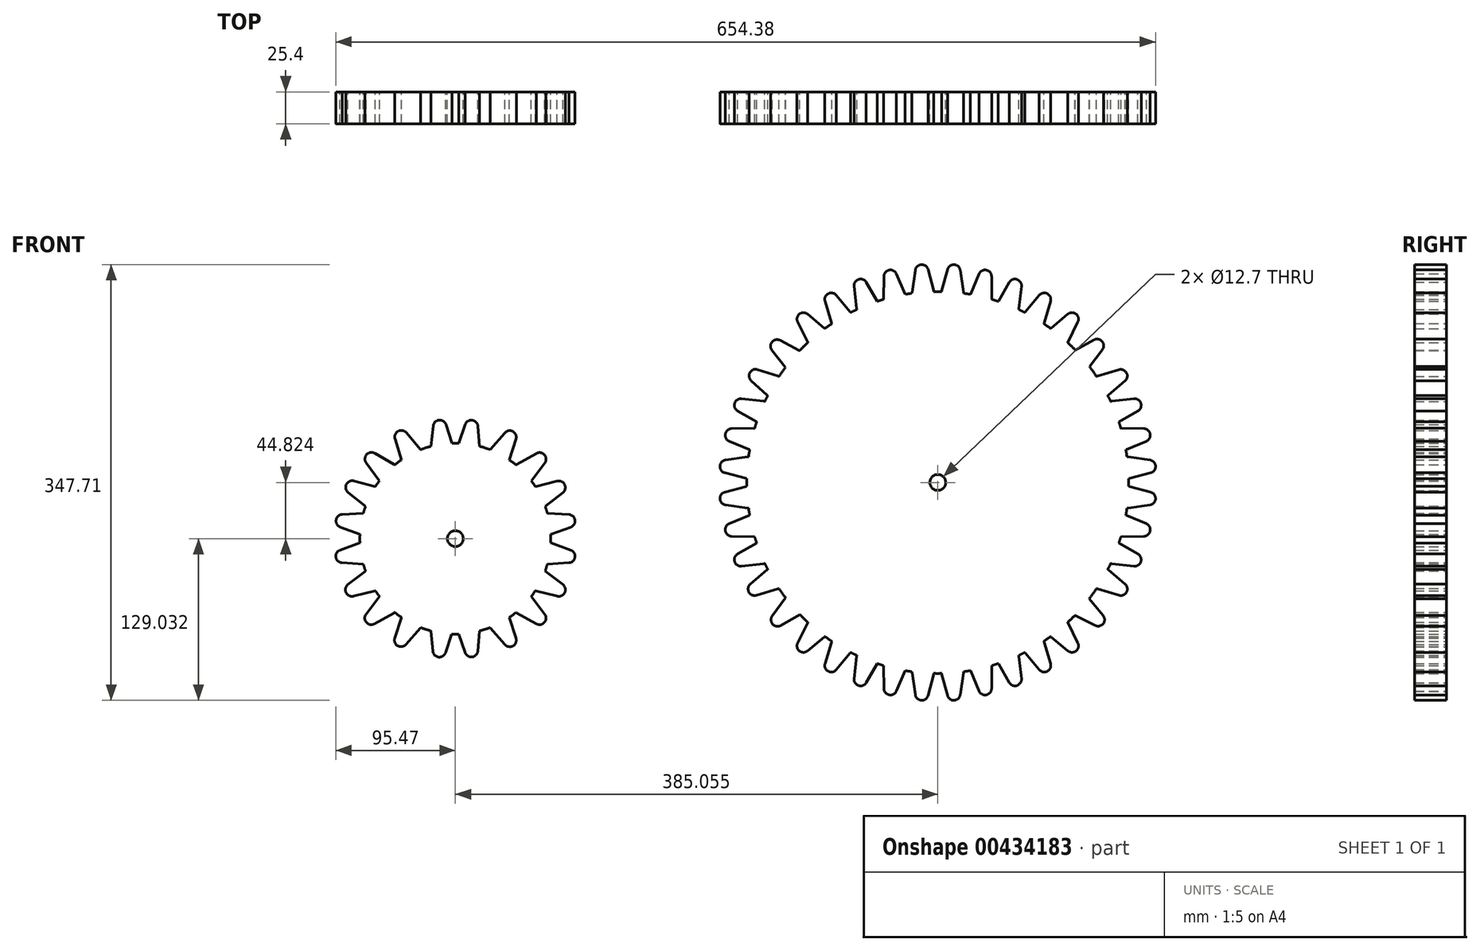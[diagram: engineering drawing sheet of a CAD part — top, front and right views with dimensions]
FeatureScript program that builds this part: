
annotation { "Feature Type Name" : "Feature", "Feature Type Description" : "" }
export const myFeature = defineFeature(function(context is Context, id is Id, definition is map)
    precondition{}
    {
        {
            var Q0;
            Q0=qCreatedBy(makeId("Front.planeOp"),FACE);
            var sketch = newSketch(context, id + "F0", { "sketchPlane" : qUnion([Q0])});
            skCircle(sketch, "E0", {"center": v(90.4, 32.98) * mm, "radius": 152.4 * mm});
            skCircle(sketch, "E1", {"center": v(90.4, 32.98) * mm, "radius": 6.35 * mm});
            skCircle(sketch, "E2", {"center": v(-294.65, -11.85) * mm, "radius": 76.2 * mm});
            skCircle(sketch, "E3", {"center": v(-294.65, -11.85) * mm, "radius": 6.35 * mm});
            skLineSegment(sketch, "E4", {"start": v(-78.98, 50.92) * mm, "end": v(-61.5, 53.51) * mm});
            skLineSegment(sketch, "E5", {"start": v(-57.15, 49.41) * mm, "end": v(-58.01, 39.52) * mm});
            skLineSegment(sketch, "E6", {"start": v(-62.8, 36.17) * mm, "end": v(-79.65, 40.7) * mm});
            skPoint(sketch, "E7.visualSharp", {"position": v(-82.74, 41.52) * mm});
            skPoint(sketch, "E8.visualSharp", {"position": v(-81.95, 50.47) * mm});
            skArc(sketch, "E9.filletArc", {"start": v(-57.15, 49.41) * mm, "mid": v(-58.33, 52.52) * mm, "end": v(-61.5, 53.51) * mm});
            skArc(sketch, "E10.filletArc", {"start": v(-62.8, 36.17) * mm, "mid": v(-59.62, 36.73) * mm, "end": v(-58.01, 39.52) * mm});
            skLineSegment(sketch, "E11", {"start": v(-66.15, 99.78) * mm, "end": v(-48.58, 97.84) * mm});
            skLineSegment(sketch, "E12", {"start": v(-45.42, 92.76) * mm, "end": v(-48.78, 83.42) * mm});
            skLineSegment(sketch, "E13", {"start": v(-54.25, 81.4) * mm, "end": v(-69.4, 90.07) * mm});
            skPoint(sketch, "E14.visualSharp", {"position": v(-72.18, 91.66) * mm});
            skArc(sketch, "E15.filletArc", {"start": v(-45.42, 92.76) * mm, "mid": v(-45.77, 96.07) * mm, "end": v(-48.58, 97.84) * mm});
            skArc(sketch, "E16.filletArc", {"start": v(-54.25, 81.4) * mm, "mid": v(-51.05, 81.13) * mm, "end": v(-48.78, 83.42) * mm});
            skLineSegment(sketch, "E17", {"start": v(-53.37, 123.14) * mm, "end": v(-37.03, 117.86) * mm});
            skLineSegment(sketch, "E18", {"start": v(-34.9, 112.33) * mm, "end": v(-39.88, 103.71) * mm});
            skLineSegment(sketch, "E19", {"start": v(-45.73, 102.79) * mm, "end": v(-58.48, 114.27) * mm});
            skPoint(sketch, "E20.visualSharp", {"position": v(-60.77, 116.34) * mm});
            skPoint(sketch, "E21.visualSharp", {"position": v(-56.3, 124.09) * mm});
            skArc(sketch, "E22.filletArc", {"start": v(-34.9, 112.33) * mm, "mid": v(-34.65, 115.6) * mm, "end": v(-37.03, 117.86) * mm});
            skArc(sketch, "E23.filletArc", {"start": v(-45.73, 102.79) * mm, "mid": v(-42.58, 101.85) * mm, "end": v(-39.88, 103.71) * mm});
            skLineSegment(sketch, "E24", {"start": v(-74.04, 75.96) * mm, "end": v(-56.37, 76.18) * mm});
            skLineSegment(sketch, "E25", {"start": v(-52.61, 71.53) * mm, "end": v(-54.8, 61.85) * mm});
            skLineSegment(sketch, "E26", {"start": v(-59.99, 59.17) * mm, "end": v(-76.08, 65.92) * mm});
            skPoint(sketch, "E27.visualSharp", {"position": v(-79.03, 67.15) * mm});
            skPoint(sketch, "E28.visualSharp", {"position": v(-77.05, 75.92) * mm});
            skArc(sketch, "E29.filletArc", {"start": v(-52.61, 71.53) * mm, "mid": v(-53.37, 74.77) * mm, "end": v(-56.37, 76.18) * mm});
            skArc(sketch, "E30.filletArc", {"start": v(-59.99, 59.17) * mm, "mid": v(-56.77, 59.3) * mm, "end": v(-54.8, 61.85) * mm});
            skLineSegment(sketch, "E31.MirrorCS", {"start": v(-7.67, 143.95) * mm, "end": v(-0.07, 150.34) * mm});
            skLineSegment(sketch, "E32.MirrorCS", {"start": v(-0.07, 156.17) * mm, "end": v(-13.44, 167.4) * mm});
            skLineSegment(sketch, "E33.MirrorCS", {"start": v(-21.43, 160.98) * mm, "end": v(-13.53, 145.17) * mm});
            skPoint(sketch, "E34.MirrorP", {"position": v(-22.77, 163.67) * mm});
            skArc(sketch, "E35.MirrorCS", {"start": v(-7.67, 143.95) * mm, "mid": v(-10.9, 143.14) * mm, "end": v(-13.53, 145.17) * mm});
            skArc(sketch, "E36.MirrorCS", {"start": v(-0.07, 156.17) * mm, "mid": v(1.3, 153.25) * mm, "end": v(-0.07, 150.34) * mm});
            skLineSegment(sketch, "E37.MirrorCS", {"start": v(10.98, 158.4) * mm, "end": v(19.58, 163.36) * mm});
            skArc(sketch, "E38.MirrorCS", {"start": v(10.98, 158.4) * mm, "mid": v(7.67, 158.16) * mm, "end": v(5.43, 160.61) * mm});
            skArc(sketch, "E39.MirrorCS", {"start": v(20.6, 169.11) * mm, "mid": v(21.43, 166) * mm, "end": v(19.58, 163.36) * mm});
            skLineSegment(sketch, "E40.MirrorCS", {"start": v(20.6, 169.11) * mm, "end": v(9.38, 182.48) * mm});
            skLineSegment(sketch, "E41.MirrorCS", {"start": v(0.4, 177.55) * mm, "end": v(5.43, 160.61) * mm});
            skPoint(sketch, "E42.MirrorP", {"position": v(-0.46, 180.43) * mm});
            skArc(sketch, "E43.MirrorCS", {"start": v(30.62, 168.8) * mm, "mid": v(27.32, 169.15) * mm, "end": v(25.55, 171.97) * mm});
            skLineSegment(sketch, "E44.MirrorCS", {"start": v(30.62, 168.8) * mm, "end": v(39.96, 172.16) * mm});
            skArc(sketch, "E45.MirrorCS", {"start": v(41.98, 177.64) * mm, "mid": v(42.25, 174.43) * mm, "end": v(39.96, 172.16) * mm});
            skLineSegment(sketch, "E46.MirrorCS", {"start": v(41.98, 177.64) * mm, "end": v(33.31, 192.78) * mm});
            skLineSegment(sketch, "E47.MirrorCS", {"start": v(23.6, 189.53) * mm, "end": v(25.55, 171.97) * mm});
            skLineSegment(sketch, "E48.MirrorCS", {"start": v(47.42, 197.43) * mm, "end": v(47.2, 179.76) * mm});
            skLineSegment(sketch, "E49.MirrorCS", {"start": v(64.2, 183.37) * mm, "end": v(57.47, 199.46) * mm});
            skArc(sketch, "E50.MirrorCS", {"start": v(64.2, 183.37) * mm, "mid": v(64.08, 180.15) * mm, "end": v(61.53, 178.18) * mm});
            skLineSegment(sketch, "E51.MirrorCS", {"start": v(51.85, 176) * mm, "end": v(61.53, 178.18) * mm});
            skArc(sketch, "E52.MirrorCS", {"start": v(51.85, 176) * mm, "mid": v(48.61, 176.75) * mm, "end": v(47.2, 179.76) * mm});
            skArc(sketch, "E53.MirrorCS", {"start": v(73.97, 180.53) * mm, "mid": v(70.86, 181.71) * mm, "end": v(69.87, 184.88) * mm});
            skLineSegment(sketch, "E54.MirrorCS", {"start": v(73.97, 180.53) * mm, "end": v(83.86, 181.4) * mm});
            skArc(sketch, "E55.MirrorCS", {"start": v(87.2, 186.17) * mm, "mid": v(86.65, 183) * mm, "end": v(83.86, 181.4) * mm});
            skLineSegment(sketch, "E56.MirrorCS", {"start": v(87.2, 186.17) * mm, "end": v(82.69, 203.03) * mm});
            skLineSegment(sketch, "E57.MirrorCS", {"start": v(72.47, 202.36) * mm, "end": v(69.87, 184.88) * mm});
            skLineSegment(sketch, "E58.MirrorCS", {"start": v(93.6, 186.17) * mm, "end": v(98.12, 203.03) * mm});
            skLineSegment(sketch, "E59.MirrorCS", {"start": v(108.35, 202.36) * mm, "end": v(110.94, 184.88) * mm});
            skArc(sketch, "E60.MirrorCS", {"start": v(106.84, 180.53) * mm, "mid": v(109.95, 181.71) * mm, "end": v(110.94, 184.88) * mm});
            skLineSegment(sketch, "E61.MirrorCS", {"start": v(106.84, 180.53) * mm, "end": v(96.95, 181.4) * mm});
            skArc(sketch, "E62.MirrorCS", {"start": v(93.6, 186.17) * mm, "mid": v(94.16, 183) * mm, "end": v(96.95, 181.4) * mm});
            skLineSegment(sketch, "E63.MirrorCS", {"start": v(133.39, 197.43) * mm, "end": v(133.6, 179.76) * mm});
            skArc(sketch, "E64.MirrorCS", {"start": v(128.96, 176) * mm, "mid": v(132.2, 176.75) * mm, "end": v(133.6, 179.76) * mm});
            skLineSegment(sketch, "E65.MirrorCS", {"start": v(128.96, 176) * mm, "end": v(119.28, 178.18) * mm});
            skArc(sketch, "E66.MirrorCS", {"start": v(116.6, 183.37) * mm, "mid": v(116.73, 180.15) * mm, "end": v(119.28, 178.18) * mm});
            skLineSegment(sketch, "E67.MirrorCS", {"start": v(116.6, 183.37) * mm, "end": v(123.35, 199.46) * mm});
            skLineSegment(sketch, "E68.MirrorCS", {"start": v(138.83, 177.64) * mm, "end": v(147.5, 192.78) * mm});
            skLineSegment(sketch, "E69.MirrorCS", {"start": v(157.21, 189.53) * mm, "end": v(155.27, 171.97) * mm});
            skArc(sketch, "E70.MirrorCS", {"start": v(150.2, 168.8) * mm, "mid": v(153.5, 169.15) * mm, "end": v(155.27, 171.97) * mm});
            skLineSegment(sketch, "E71.MirrorCS", {"start": v(150.2, 168.8) * mm, "end": v(140.85, 172.16) * mm});
            skArc(sketch, "E72.MirrorCS", {"start": v(138.83, 177.64) * mm, "mid": v(138.56, 174.43) * mm, "end": v(140.85, 172.16) * mm});
            skLineSegment(sketch, "E73.MirrorCS", {"start": v(160.22, 169.11) * mm, "end": v(171.43, 182.48) * mm});
            skLineSegment(sketch, "E74.MirrorCS", {"start": v(180.42, 177.55) * mm, "end": v(175.38, 160.61) * mm});
            skArc(sketch, "E75.MirrorCS", {"start": v(169.83, 158.4) * mm, "mid": v(173.14, 158.16) * mm, "end": v(175.38, 160.61) * mm});
            skLineSegment(sketch, "E76.MirrorCS", {"start": v(169.83, 158.4) * mm, "end": v(161.23, 163.36) * mm});
            skArc(sketch, "E77.MirrorCS", {"start": v(160.22, 169.11) * mm, "mid": v(159.38, 166) * mm, "end": v(161.23, 163.36) * mm});
            skArc(sketch, "E78.MirrorCS", {"start": v(180.88, 156.17) * mm, "mid": v(179.52, 153.25) * mm, "end": v(180.88, 150.34) * mm});
            skLineSegment(sketch, "E79.MirrorCS", {"start": v(180.88, 156.17) * mm, "end": v(194.25, 167.4) * mm});
            skLineSegment(sketch, "E80.MirrorCS", {"start": v(202.24, 160.98) * mm, "end": v(194.34, 145.17) * mm});
            skArc(sketch, "E81.MirrorCS", {"start": v(188.48, 143.95) * mm, "mid": v(191.7, 143.14) * mm, "end": v(194.34, 145.17) * mm});
            skLineSegment(sketch, "E82.MirrorCS", {"start": v(188.48, 143.95) * mm, "end": v(180.88, 150.34) * mm});
            skLineSegment(sketch, "E83.MirrorCS", {"start": v(234.98, 122.99) * mm, "end": v(218.04, 117.95) * mm});
            skLineSegment(sketch, "E84.MirrorCS", {"start": v(226.54, 102.79) * mm, "end": v(239.91, 114) * mm});
            skArc(sketch, "E85.MirrorCS", {"start": v(226.54, 102.79) * mm, "mid": v(223.43, 101.95) * mm, "end": v(220.8, 103.8) * mm});
            skArc(sketch, "E86.MirrorCS", {"start": v(215.83, 112.4) * mm, "mid": v(215.6, 115.71) * mm, "end": v(218.04, 117.95) * mm});
            skLineSegment(sketch, "E87.MirrorCS", {"start": v(246.96, 99.78) * mm, "end": v(229.4, 97.84) * mm});
            skPoint(sketch, "E88.MirrorP", {"position": v(252.99, 91.66) * mm});
            skLineSegment(sketch, "E89.MirrorCS", {"start": v(235.07, 81.4) * mm, "end": v(250.21, 90.07) * mm});
            skArc(sketch, "E90.MirrorCS", {"start": v(235.07, 81.4) * mm, "mid": v(231.86, 81.13) * mm, "end": v(229.59, 83.42) * mm});
            skLineSegment(sketch, "E91.MirrorCS", {"start": v(226.23, 92.76) * mm, "end": v(229.59, 83.42) * mm});
            skArc(sketch, "E92.MirrorCS", {"start": v(226.23, 92.76) * mm, "mid": v(226.58, 96.07) * mm, "end": v(229.4, 97.84) * mm});
            skArc(sketch, "E93.MirrorCS", {"start": v(233.42, 71.53) * mm, "mid": v(234.18, 74.77) * mm, "end": v(237.19, 76.18) * mm});
            skLineSegment(sketch, "E94.MirrorCS", {"start": v(254.86, 75.96) * mm, "end": v(237.19, 76.18) * mm});
            skLineSegment(sketch, "E95.MirrorCS", {"start": v(240.8, 59.17) * mm, "end": v(256.9, 65.92) * mm});
            skArc(sketch, "E96.MirrorCS", {"start": v(240.8, 59.17) * mm, "mid": v(237.58, 59.3) * mm, "end": v(235.6, 61.85) * mm});
            skLineSegment(sketch, "E97.MirrorCS", {"start": v(233.42, 71.53) * mm, "end": v(235.6, 61.85) * mm});
            skArc(sketch, "E98.MirrorCS", {"start": v(237.96, 49.41) * mm, "mid": v(239.14, 52.52) * mm, "end": v(242.31, 53.51) * mm});
            skLineSegment(sketch, "E99.MirrorCS", {"start": v(259.8, 50.92) * mm, "end": v(242.31, 53.51) * mm});
            skLineSegment(sketch, "E100.MirrorCS", {"start": v(243.6, 36.17) * mm, "end": v(260.46, 40.7) * mm});
            skArc(sketch, "E101.MirrorCS", {"start": v(243.6, 36.17) * mm, "mid": v(240.43, 36.73) * mm, "end": v(238.82, 39.52) * mm});
            skLineSegment(sketch, "E102.MirrorCS", {"start": v(237.96, 49.41) * mm, "end": v(238.82, 39.52) * mm});
            skArc(sketch, "E103.MirrorCS", {"start": v(-62.8, 29.78) * mm, "mid": v(-59.62, 29.22) * mm, "end": v(-58.01, 26.43) * mm});
            skLineSegment(sketch, "E104.MirrorCS", {"start": v(-57.15, 16.54) * mm, "end": v(-58.01, 26.43) * mm});
            skArc(sketch, "E105.MirrorCS", {"start": v(-57.15, 16.54) * mm, "mid": v(-58.33, 13.43) * mm, "end": v(-61.5, 12.44) * mm});
            skLineSegment(sketch, "E106.MirrorCS", {"start": v(-78.98, 15.04) * mm, "end": v(-61.5, 12.44) * mm});
            skPoint(sketch, "E107.MirrorP", {"position": v(-81.95, 15.48) * mm});
            skPoint(sketch, "E108.MirrorP", {"position": v(-82.74, 24.43) * mm});
            skLineSegment(sketch, "E109.MirrorCS", {"start": v(-62.8, 29.78) * mm, "end": v(-79.65, 25.26) * mm});
            skLineSegment(sketch, "E110.MirrorCS", {"start": v(-59.99, 6.78) * mm, "end": v(-76.08, 0.04) * mm});
            skPoint(sketch, "E111.MirrorP", {"position": v(-79.03, -1.2) * mm});
            skLineSegment(sketch, "E112.MirrorCS", {"start": v(-74.04, -10) * mm, "end": v(-56.37, -10.23) * mm});
            skArc(sketch, "E113.MirrorCS", {"start": v(-52.61, -5.58) * mm, "mid": v(-53.37, -8.82) * mm, "end": v(-56.37, -10.23) * mm});
            skLineSegment(sketch, "E114.MirrorCS", {"start": v(-52.61, -5.58) * mm, "end": v(-54.8, 4.1) * mm});
            skArc(sketch, "E115.MirrorCS", {"start": v(-59.99, 6.78) * mm, "mid": v(-56.77, 6.65) * mm, "end": v(-54.8, 4.1) * mm});
            skArc(sketch, "E116.MirrorCS", {"start": v(-54.25, -15.45) * mm, "mid": v(-51.05, -15.18) * mm, "end": v(-48.78, -17.47) * mm});
            skLineSegment(sketch, "E117.MirrorCS", {"start": v(-45.42, -26.8) * mm, "end": v(-48.78, -17.47) * mm});
            skArc(sketch, "E118.MirrorCS", {"start": v(-45.42, -26.8) * mm, "mid": v(-45.77, -30.11) * mm, "end": v(-48.58, -31.88) * mm});
            skLineSegment(sketch, "E119.MirrorCS", {"start": v(-66.15, -33.83) * mm, "end": v(-48.58, -31.88) * mm});
            skPoint(sketch, "E120.MirrorP", {"position": v(-69.14, -34.16) * mm});
            skPoint(sketch, "E121.MirrorP", {"position": v(-72.18, -25.7) * mm});
            skLineSegment(sketch, "E122.MirrorCS", {"start": v(-54.25, -15.45) * mm, "end": v(-69.4, -24.12) * mm});
            skArc(sketch, "E123.MirrorCS", {"start": v(-45.73, -36.84) * mm, "mid": v(-42.62, -36) * mm, "end": v(-39.98, -37.85) * mm});
            skArc(sketch, "E124.MirrorCS", {"start": v(-35.02, -46.45) * mm, "mid": v(-34.78, -49.76) * mm, "end": v(-37.23, -52) * mm});
            skLineSegment(sketch, "E125.MirrorCS", {"start": v(-54.17, -57.04) * mm, "end": v(-37.23, -52) * mm});
            skLineSegment(sketch, "E126.MirrorCS", {"start": v(-45.73, -36.84) * mm, "end": v(-59.1, -48.05) * mm});
            skArc(sketch, "E127.MirrorCS", {"start": v(-7.67, -78) * mm, "mid": v(-10.9, -77.2) * mm, "end": v(-13.53, -79.22) * mm});
            skLineSegment(sketch, "E128.MirrorCS", {"start": v(-7.67, -78) * mm, "end": v(-0.07, -84.38) * mm});
            skArc(sketch, "E129.MirrorCS", {"start": v(-0.07, -90.22) * mm, "mid": v(1.3, -87.3) * mm, "end": v(-0.07, -84.38) * mm});
            skLineSegment(sketch, "E130.MirrorCS", {"start": v(-0.07, -90.22) * mm, "end": v(-13.44, -101.44) * mm});
            skLineSegment(sketch, "E131.MirrorCS", {"start": v(-35.02, -46.45) * mm, "end": v(-39.98, -37.85) * mm});
            skLineSegment(sketch, "E132.MirrorCS", {"start": v(-21.43, -95.03) * mm, "end": v(-13.53, -79.22) * mm});
            skArc(sketch, "E133.MirrorCS", {"start": v(10.98, -92.45) * mm, "mid": v(7.67, -92.2) * mm, "end": v(5.43, -94.66) * mm});
            skLineSegment(sketch, "E134.MirrorCS", {"start": v(0.4, -111.6) * mm, "end": v(5.43, -94.66) * mm});
            skLineSegment(sketch, "E135.MirrorCS", {"start": v(20.6, -103.16) * mm, "end": v(9.38, -116.53) * mm});
            skArc(sketch, "E136.MirrorCS", {"start": v(20.6, -103.16) * mm, "mid": v(21.43, -100.05) * mm, "end": v(19.58, -97.41) * mm});
            skLineSegment(sketch, "E137.MirrorCS", {"start": v(10.98, -92.45) * mm, "end": v(19.58, -97.41) * mm});
            skArc(sketch, "E138.MirrorCS", {"start": v(30.62, -102.85) * mm, "mid": v(27.32, -103.2) * mm, "end": v(25.55, -106.01) * mm});
            skLineSegment(sketch, "E139.MirrorCS", {"start": v(30.62, -102.85) * mm, "end": v(39.96, -106.2) * mm});
            skArc(sketch, "E140.MirrorCS", {"start": v(41.98, -111.68) * mm, "mid": v(42.25, -108.48) * mm, "end": v(39.96, -106.2) * mm});
            skLineSegment(sketch, "E141.MirrorCS", {"start": v(41.98, -111.68) * mm, "end": v(33.31, -126.83) * mm});
            skArc(sketch, "E142.MirrorCS", {"start": v(28.72, -128.53) * mm, "mid": v(31.32, -128.52) * mm, "end": v(33.31, -126.83) * mm});
            skLineSegment(sketch, "E143.MirrorCS", {"start": v(23.6, -123.58) * mm, "end": v(25.55, -106.01) * mm});
            skLineSegment(sketch, "E144.MirrorCS", {"start": v(47.42, -131.47) * mm, "end": v(47.2, -113.8) * mm});
            skArc(sketch, "E145.MirrorCS", {"start": v(51.85, -110.04) * mm, "mid": v(48.61, -110.8) * mm, "end": v(47.2, -113.8) * mm});
            skLineSegment(sketch, "E146.MirrorCS", {"start": v(51.85, -110.04) * mm, "end": v(61.53, -112.23) * mm});
            skArc(sketch, "E147.MirrorCS", {"start": v(64.2, -117.42) * mm, "mid": v(64.08, -114.2) * mm, "end": v(61.53, -112.23) * mm});
            skLineSegment(sketch, "E148.MirrorCS", {"start": v(64.2, -117.42) * mm, "end": v(57.47, -133.51) * mm});
            skLineSegment(sketch, "E149.MirrorCS", {"start": v(72.47, -136.41) * mm, "end": v(69.87, -118.93) * mm});
            skArc(sketch, "E150.MirrorCS", {"start": v(73.97, -114.58) * mm, "mid": v(70.86, -115.76) * mm, "end": v(69.87, -118.93) * mm});
            skLineSegment(sketch, "E151.MirrorCS", {"start": v(73.97, -114.58) * mm, "end": v(83.86, -115.44) * mm});
            skArc(sketch, "E152.MirrorCS", {"start": v(87.2, -120.22) * mm, "mid": v(86.65, -117.05) * mm, "end": v(83.86, -115.44) * mm});
            skLineSegment(sketch, "E153.MirrorCS", {"start": v(87.2, -120.22) * mm, "end": v(82.69, -137.08) * mm});
            skLineSegment(sketch, "E154.MirrorCS", {"start": v(93.6, -120.22) * mm, "end": v(98.12, -137.08) * mm});
            skArc(sketch, "E155.MirrorCS", {"start": v(93.6, -120.22) * mm, "mid": v(94.16, -117.05) * mm, "end": v(96.95, -115.44) * mm});
            skLineSegment(sketch, "E156.MirrorCS", {"start": v(106.84, -114.58) * mm, "end": v(96.95, -115.44) * mm});
            skArc(sketch, "E157.MirrorCS", {"start": v(106.84, -114.58) * mm, "mid": v(109.95, -115.76) * mm, "end": v(110.94, -118.93) * mm});
            skLineSegment(sketch, "E158.MirrorCS", {"start": v(108.35, -136.41) * mm, "end": v(110.94, -118.93) * mm});
            skArc(sketch, "E159.MirrorCS", {"start": v(127.7, -135.76) * mm, "mid": v(125.11, -135.43) * mm, "end": v(123.35, -133.51) * mm});
            skLineSegment(sketch, "E160.MirrorCS", {"start": v(133.39, -131.47) * mm, "end": v(133.6, -113.8) * mm});
            skArc(sketch, "E161.MirrorCS", {"start": v(128.96, -110.04) * mm, "mid": v(132.2, -110.8) * mm, "end": v(133.6, -113.8) * mm});
            skLineSegment(sketch, "E162.MirrorCS", {"start": v(128.96, -110.04) * mm, "end": v(119.28, -112.23) * mm});
            skArc(sketch, "E163.MirrorCS", {"start": v(116.6, -117.42) * mm, "mid": v(116.73, -114.2) * mm, "end": v(119.28, -112.23) * mm});
            skLineSegment(sketch, "E164.MirrorCS", {"start": v(116.6, -117.42) * mm, "end": v(123.35, -133.51) * mm});
            skLineSegment(sketch, "E165.MirrorCS", {"start": v(152.1, -128.53) * mm, "end": v(154.72, -127.58) * mm});
            skArc(sketch, "E166.MirrorCS", {"start": v(150.2, -102.85) * mm, "mid": v(153.5, -103.2) * mm, "end": v(155.27, -106.01) * mm});
            skArc(sketch, "E167.MirrorCS", {"start": v(138.83, -111.68) * mm, "mid": v(138.56, -108.48) * mm, "end": v(140.85, -106.2) * mm});
            skLineSegment(sketch, "E168.MirrorCS", {"start": v(138.83, -111.68) * mm, "end": v(147.5, -126.83) * mm});
            skLineSegment(sketch, "E169.MirrorCS", {"start": v(160.22, -103.16) * mm, "end": v(171.43, -116.53) * mm});
            skLineSegment(sketch, "E170.MirrorCS", {"start": v(180.42, -111.6) * mm, "end": v(175.38, -94.66) * mm});
            skArc(sketch, "E171.MirrorCS", {"start": v(169.83, -92.45) * mm, "mid": v(173.14, -92.2) * mm, "end": v(175.38, -94.66) * mm});
            skArc(sketch, "E172.MirrorCS", {"start": v(160.22, -103.16) * mm, "mid": v(159.38, -100.05) * mm, "end": v(161.23, -97.41) * mm});
            skLineSegment(sketch, "E173.MirrorCS", {"start": v(180.88, -90.22) * mm, "end": v(194.25, -101.44) * mm});
            skArc(sketch, "E174.MirrorCS", {"start": v(180.88, -90.22) * mm, "mid": v(179.52, -87.3) * mm, "end": v(180.88, -84.38) * mm});
            skLineSegment(sketch, "E175.MirrorCS", {"start": v(188.48, -78) * mm, "end": v(180.88, -84.38) * mm});
            skArc(sketch, "E176.MirrorCS", {"start": v(188.48, -78) * mm, "mid": v(191.7, -77.2) * mm, "end": v(194.34, -79.22) * mm});
            skLineSegment(sketch, "E177.MirrorCS", {"start": v(202.24, -95.03) * mm, "end": v(194.34, -79.22) * mm});
            skLineSegment(sketch, "E178.MirrorCS", {"start": v(234.98, -57.04) * mm, "end": v(218.04, -52) * mm});
            skLineSegment(sketch, "E179.MirrorCS", {"start": v(226.54, -36.84) * mm, "end": v(239.91, -48.05) * mm});
            skArc(sketch, "E180.MirrorCS", {"start": v(226.54, -36.84) * mm, "mid": v(223.43, -36) * mm, "end": v(220.8, -37.85) * mm});
            skLineSegment(sketch, "E181.MirrorCS", {"start": v(215.83, -46.45) * mm, "end": v(220.8, -37.85) * mm});
            skArc(sketch, "E182.MirrorCS", {"start": v(215.83, -46.45) * mm, "mid": v(215.6, -49.76) * mm, "end": v(218.04, -52) * mm});
            skLineSegment(sketch, "E183.MirrorCS", {"start": v(246.96, -33.83) * mm, "end": v(229.4, -31.88) * mm});
            skArc(sketch, "E184.MirrorCS", {"start": v(226.23, -26.8) * mm, "mid": v(226.58, -30.11) * mm, "end": v(229.4, -31.88) * mm});
            skLineSegment(sketch, "E185.MirrorCS", {"start": v(226.23, -26.8) * mm, "end": v(229.59, -17.47) * mm});
            skArc(sketch, "E186.MirrorCS", {"start": v(235.07, -15.45) * mm, "mid": v(231.86, -15.18) * mm, "end": v(229.59, -17.47) * mm});
            skLineSegment(sketch, "E187.MirrorCS", {"start": v(235.07, -15.45) * mm, "end": v(250.21, -24.12) * mm});
            skPoint(sketch, "E188.MirrorP", {"position": v(249.95, -34.16) * mm});
            skLineSegment(sketch, "E189.MirrorCS", {"start": v(254.86, -10) * mm, "end": v(237.19, -10.23) * mm});
            skArc(sketch, "E190.MirrorCS", {"start": v(233.42, -5.58) * mm, "mid": v(234.18, -8.82) * mm, "end": v(237.19, -10.23) * mm});
            skLineSegment(sketch, "E191.MirrorCS", {"start": v(240.8, 6.78) * mm, "end": v(256.9, 0.04) * mm});
            skLineSegment(sketch, "E192.MirrorCS", {"start": v(259.8, 15.04) * mm, "end": v(242.31, 12.44) * mm});
            skLineSegment(sketch, "E193.MirrorCS", {"start": v(237.96, 16.54) * mm, "end": v(238.82, 26.43) * mm});
            skArc(sketch, "E194.MirrorCS", {"start": v(243.6, 29.78) * mm, "mid": v(240.43, 29.22) * mm, "end": v(238.82, 26.43) * mm});
            skLineSegment(sketch, "E195.MirrorCS", {"start": v(243.6, 29.78) * mm, "end": v(260.46, 25.26) * mm});
            skLineSegment(sketch, "E196.MirrorCS", {"start": v(150.2, -102.85) * mm, "end": v(140.85, -106.2) * mm});
            skLineSegment(sketch, "E197.MirrorCS", {"start": v(169.83, -92.45) * mm, "end": v(161.23, -97.41) * mm});
            skLineSegment(sketch, "E198.MirrorCS", {"start": v(157.21, -123.58) * mm, "end": v(155.27, -106.01) * mm});
            skArc(sketch, "E199.MirrorCS", {"start": v(237.96, 16.54) * mm, "mid": v(239.14, 13.43) * mm, "end": v(242.31, 12.44) * mm});
            skLineSegment(sketch, "E200.MirrorCS", {"start": v(233.42, -5.58) * mm, "end": v(235.6, 4.1) * mm});
            skArc(sketch, "E201.MirrorCS", {"start": v(240.8, 6.78) * mm, "mid": v(237.58, 6.65) * mm, "end": v(235.6, 4.1) * mm});
            skLineSegment(sketch, "E202", {"start": v(-384.91, 7.54) * mm, "end": v(-367.48, 8.47) * mm});
            skLineSegment(sketch, "E203", {"start": v(-363.53, 4) * mm, "end": v(-365.25, -5.78) * mm});
            skLineSegment(sketch, "E204", {"start": v(-370.35, -8.69) * mm, "end": v(-386.54, -2.57) * mm});
            skPoint(sketch, "E205.visualSharp", {"position": v(-389.5, -1.46) * mm});
            skPoint(sketch, "E206.visualSharp", {"position": v(-387.93, 7.38) * mm});
            skArc(sketch, "E207.filletArc", {"start": v(-363.53, 4) * mm, "mid": v(-364.43, 7.19) * mm, "end": v(-367.48, 8.47) * mm});
            skArc(sketch, "E208.filletArc", {"start": v(-370.35, -8.69) * mm, "mid": v(-367.12, -8.43) * mm, "end": v(-365.25, -5.78) * mm});
            skLineSegment(sketch, "E209", {"start": v(-302.17, 79.14) * mm, "end": v(-296.85, 62.3) * mm});
            skLineSegment(sketch, "E210", {"start": v(-300.15, 57.37) * mm, "end": v(-310.03, 56.5) * mm});
            skLineSegment(sketch, "E211", {"start": v(-314.15, 60.68) * mm, "end": v(-312.37, 78.14) * mm});
            skPoint(sketch, "E212.visualSharp", {"position": v(-312.05, 81.27) * mm});
            skPoint(sketch, "E213.visualSharp", {"position": v(-303.09, 82.05) * mm});
            skArc(sketch, "E214.filletArc", {"start": v(-300.15, 57.37) * mm, "mid": v(-297.31, 59.04) * mm, "end": v(-296.85, 62.3) * mm});
            skArc(sketch, "E215.filletArc", {"start": v(-314.15, 60.68) * mm, "mid": v(-313.07, 57.62) * mm, "end": v(-310.03, 56.5) * mm});
            skLineSegment(sketch, "E216", {"start": v(-358.91, 56.25) * mm, "end": v(-343.72, 47.43) * mm});
            skLineSegment(sketch, "E217", {"start": v(-342.84, 41.55) * mm, "end": v(-349.59, 34.25) * mm});
            skLineSegment(sketch, "E218", {"start": v(-355.45, 34.58) * mm, "end": v(-365.8, 48.66) * mm});
            skPoint(sketch, "E219.visualSharp", {"position": v(-367.65, 51.2) * mm});
            skPoint(sketch, "E220.visualSharp", {"position": v(-361.55, 57.78) * mm});
            skArc(sketch, "E221.filletArc", {"start": v(-342.84, 41.55) * mm, "mid": v(-341.86, 44.7) * mm, "end": v(-343.72, 47.43) * mm});
            skArc(sketch, "E222.filletArc", {"start": v(-355.45, 34.58) * mm, "mid": v(-352.6, 33.04) * mm, "end": v(-349.59, 34.25) * mm});
            skLineSegment(sketch, "E223", {"start": v(-333.8, 72.69) * mm, "end": v(-322.4, 59.2) * mm});
            skLineSegment(sketch, "E224", {"start": v(-323.54, 53.36) * mm, "end": v(-332.34, 48.75) * mm});
            skLineSegment(sketch, "E225", {"start": v(-337.76, 51.02) * mm, "end": v(-342.82, 67.84) * mm});
            skPoint(sketch, "E226.visualSharp", {"position": v(-343.73, 70.85) * mm});
            skPoint(sketch, "E227.visualSharp", {"position": v(-335.77, 75.02) * mm});
            skArc(sketch, "E228.filletArc", {"start": v(-323.54, 53.36) * mm, "mid": v(-321.57, 56) * mm, "end": v(-322.4, 59.2) * mm});
            skArc(sketch, "E229.filletArc", {"start": v(-337.76, 51.02) * mm, "mid": v(-335.58, 48.6) * mm, "end": v(-332.34, 48.75) * mm});
            skLineSegment(sketch, "E230", {"start": v(-375.59, 34.19) * mm, "end": v(-358.66, 29.72) * mm});
            skLineSegment(sketch, "E231", {"start": v(-356.25, 24.27) * mm, "end": v(-360.85, 15.46) * mm});
            skLineSegment(sketch, "E232", {"start": v(-366.6, 14.24) * mm, "end": v(-380.22, 25.05) * mm});
            skPoint(sketch, "E233.visualSharp", {"position": v(-382.69, 27) * mm});
            skPoint(sketch, "E234.visualSharp", {"position": v(-378.53, 34.96) * mm});
            skArc(sketch, "E235.filletArc", {"start": v(-356.25, 24.27) * mm, "mid": v(-356.14, 27.57) * mm, "end": v(-358.66, 29.72) * mm});
            skArc(sketch, "E236.filletArc", {"start": v(-366.6, 14.24) * mm, "mid": v(-363.44, 13.5) * mm, "end": v(-360.85, 15.46) * mm});
            skLineSegment(sketch, "E237.MirrorCS", {"start": v(-286.86, 79.07) * mm, "end": v(-292.45, 62.3) * mm});
            skArc(sketch, "E238.MirrorCS", {"start": v(-289.17, 57.3) * mm, "mid": v(-292.02, 59.01) * mm, "end": v(-292.45, 62.3) * mm});
            skLineSegment(sketch, "E239.MirrorCS", {"start": v(-289.17, 57.3) * mm, "end": v(-279.28, 56.44) * mm});
            skArc(sketch, "E240.MirrorCS", {"start": v(-275.15, 60.57) * mm, "mid": v(-276.25, 57.54) * mm, "end": v(-279.28, 56.44) * mm});
            skLineSegment(sketch, "E241.MirrorCS", {"start": v(-275.15, 60.57) * mm, "end": v(-276.67, 77.95) * mm});
            skPoint(sketch, "E242.MirrorP", {"position": v(-276.95, 81.14) * mm});
            skLineSegment(sketch, "E243.MirrorCS", {"start": v(-251.54, 51.02) * mm, "end": v(-246.24, 67.65) * mm});
            skLineSegment(sketch, "E244.MirrorCS", {"start": v(-265.73, 53.42) * mm, "end": v(-256.94, 48.8) * mm});
            skArc(sketch, "E245.MirrorCS", {"start": v(-265.73, 53.42) * mm, "mid": v(-267.7, 56.09) * mm, "end": v(-266.83, 59.3) * mm});
            skLineSegment(sketch, "E246.MirrorCS", {"start": v(-255.21, 72.6) * mm, "end": v(-266.83, 59.3) * mm});
            skLineSegment(sketch, "E247.MirrorCS", {"start": v(-230.08, 56.15) * mm, "end": v(-245.49, 47.5) * mm});
            skArc(sketch, "E248.MirrorCS", {"start": v(-251.54, 51.02) * mm, "mid": v(-253.73, 48.65) * mm, "end": v(-256.94, 48.8) * mm});
            skLineSegment(sketch, "E249.MirrorCS", {"start": v(-233.85, 34.58) * mm, "end": v(-223.3, 48.48) * mm});
            skArc(sketch, "E250.MirrorCS", {"start": v(-233.85, 34.58) * mm, "mid": v(-236.7, 33.08) * mm, "end": v(-239.68, 34.3) * mm});
            skLineSegment(sketch, "E251.MirrorCS", {"start": v(-246.42, 41.59) * mm, "end": v(-239.68, 34.3) * mm});
            skArc(sketch, "E252.MirrorCS", {"start": v(-246.42, 41.59) * mm, "mid": v(-247.39, 44.77) * mm, "end": v(-245.49, 47.5) * mm});
            skLineSegment(sketch, "E253.MirrorCS", {"start": v(-213.41, 34.07) * mm, "end": v(-230.55, 29.76) * mm});
            skArc(sketch, "E254.MirrorCS", {"start": v(-233, 24.3) * mm, "mid": v(-233.1, 27.62) * mm, "end": v(-230.55, 29.76) * mm});
            skLineSegment(sketch, "E255.MirrorCS", {"start": v(-233, 24.3) * mm, "end": v(-228.4, 15.5) * mm});
            skArc(sketch, "E256.MirrorCS", {"start": v(-222.7, 14.24) * mm, "mid": v(-225.84, 13.54) * mm, "end": v(-228.4, 15.5) * mm});
            skLineSegment(sketch, "E257.MirrorCS", {"start": v(-222.7, 14.24) * mm, "end": v(-208.87, 24.89) * mm});
            skLineSegment(sketch, "E258.MirrorCS", {"start": v(-204.1, 7.41) * mm, "end": v(-221.75, 8.47) * mm});
            skArc(sketch, "E259.MirrorCS", {"start": v(-225.73, 4) * mm, "mid": v(-224.82, 7.2) * mm, "end": v(-221.75, 8.47) * mm});
            skLineSegment(sketch, "E260.MirrorCS", {"start": v(-225.73, 4) * mm, "end": v(-224, -5.77) * mm});
            skArc(sketch, "E261.MirrorCS", {"start": v(-218.95, -8.69) * mm, "mid": v(-222.16, -8.4) * mm, "end": v(-224, -5.77) * mm});
            skLineSegment(sketch, "E262.MirrorCS", {"start": v(-218.95, -8.69) * mm, "end": v(-202.55, -2.72) * mm});
            skLineSegment(sketch, "E263.MirrorCS", {"start": v(-370.35, -15.01) * mm, "end": v(-386.75, -20.98) * mm});
            skArc(sketch, "E264.MirrorCS", {"start": v(-370.35, -15.01) * mm, "mid": v(-367.14, -15.3) * mm, "end": v(-365.3, -17.93) * mm});
            skLineSegment(sketch, "E265.MirrorCS", {"start": v(-363.57, -27.7) * mm, "end": v(-365.3, -17.93) * mm});
            skArc(sketch, "E266.MirrorCS", {"start": v(-363.57, -27.7) * mm, "mid": v(-364.48, -30.9) * mm, "end": v(-367.55, -32.17) * mm});
            skLineSegment(sketch, "E267.MirrorCS", {"start": v(-385.2, -31.1) * mm, "end": v(-367.55, -32.17) * mm});
            skLineSegment(sketch, "E268.MirrorCS", {"start": v(-366.6, -37.94) * mm, "end": v(-380.43, -48.58) * mm});
            skArc(sketch, "E269.MirrorCS", {"start": v(-366.6, -37.94) * mm, "mid": v(-363.46, -37.24) * mm, "end": v(-360.9, -39.2) * mm});
            skLineSegment(sketch, "E270.MirrorCS", {"start": v(-356.3, -48) * mm, "end": v(-360.9, -39.2) * mm});
            skArc(sketch, "E271.MirrorCS", {"start": v(-356.3, -48) * mm, "mid": v(-356.2, -51.32) * mm, "end": v(-358.75, -53.45) * mm});
            skLineSegment(sketch, "E272.MirrorCS", {"start": v(-375.89, -57.77) * mm, "end": v(-358.75, -53.45) * mm});
            skArc(sketch, "E273.MirrorCS", {"start": v(-355.45, -58.28) * mm, "mid": v(-352.6, -56.78) * mm, "end": v(-349.62, -58) * mm});
            skLineSegment(sketch, "E274.MirrorCS", {"start": v(-355.45, -58.28) * mm, "end": v(-366, -72.18) * mm});
            skLineSegment(sketch, "E275.MirrorCS", {"start": v(-359.22, -79.85) * mm, "end": v(-343.81, -71.2) * mm});
            skArc(sketch, "E276.MirrorCS", {"start": v(-342.88, -65.28) * mm, "mid": v(-341.91, -68.46) * mm, "end": v(-343.81, -71.2) * mm});
            skLineSegment(sketch, "E277.MirrorCS", {"start": v(-342.88, -65.28) * mm, "end": v(-349.62, -58) * mm});
            skArc(sketch, "E278.MirrorCS", {"start": v(-337.76, -74.72) * mm, "mid": v(-335.57, -72.35) * mm, "end": v(-332.36, -72.5) * mm});
            skLineSegment(sketch, "E279.MirrorCS", {"start": v(-337.76, -74.72) * mm, "end": v(-343.06, -91.35) * mm});
            skLineSegment(sketch, "E280.MirrorCS", {"start": v(-334.09, -96.3) * mm, "end": v(-322.47, -83) * mm});
            skArc(sketch, "E281.MirrorCS", {"start": v(-323.57, -77.11) * mm, "mid": v(-321.6, -79.79) * mm, "end": v(-322.47, -83) * mm});
            skLineSegment(sketch, "E282.MirrorCS", {"start": v(-323.57, -77.11) * mm, "end": v(-332.36, -72.5) * mm});
            skArc(sketch, "E283.MirrorCS", {"start": v(-314.15, -84.27) * mm, "mid": v(-313.05, -81.24) * mm, "end": v(-310.02, -80.14) * mm});
            skLineSegment(sketch, "E284.MirrorCS", {"start": v(-300.13, -81) * mm, "end": v(-310.02, -80.14) * mm});
            skArc(sketch, "E285.MirrorCS", {"start": v(-300.13, -81) * mm, "mid": v(-297.28, -82.7) * mm, "end": v(-296.85, -86) * mm});
            skLineSegment(sketch, "E286.MirrorCS", {"start": v(-302.44, -102.77) * mm, "end": v(-296.85, -86) * mm});
            skPoint(sketch, "E287.MirrorP", {"position": v(-303.4, -105.62) * mm});
            skLineSegment(sketch, "E288.MirrorCS", {"start": v(-314.15, -84.27) * mm, "end": v(-312.63, -101.65) * mm});
            skArc(sketch, "E289.MirrorCS", {"start": v(-289.17, -81) * mm, "mid": v(-292.02, -82.7) * mm, "end": v(-292.45, -86) * mm});
            skLineSegment(sketch, "E290.MirrorCS", {"start": v(-289.17, -81) * mm, "end": v(-279.28, -80.14) * mm});
            skArc(sketch, "E291.MirrorCS", {"start": v(-275.15, -84.27) * mm, "mid": v(-276.25, -81.24) * mm, "end": v(-279.28, -80.14) * mm});
            skLineSegment(sketch, "E292.MirrorCS", {"start": v(-275.15, -84.27) * mm, "end": v(-276.67, -101.65) * mm});
            skLineSegment(sketch, "E293.MirrorCS", {"start": v(-286.86, -102.77) * mm, "end": v(-292.45, -86) * mm});
            skArc(sketch, "E294.MirrorCS", {"start": v(-265.73, -77.11) * mm, "mid": v(-267.7, -79.79) * mm, "end": v(-266.83, -83) * mm});
            skLineSegment(sketch, "E295.MirrorCS", {"start": v(-265.73, -77.11) * mm, "end": v(-256.94, -72.5) * mm});
            skArc(sketch, "E296.MirrorCS", {"start": v(-251.54, -74.72) * mm, "mid": v(-253.73, -72.35) * mm, "end": v(-256.94, -72.5) * mm});
            skLineSegment(sketch, "E297.MirrorCS", {"start": v(-255.21, -96.3) * mm, "end": v(-266.83, -83) * mm});
            skLineSegment(sketch, "E298.MirrorCS", {"start": v(-246.42, -65.28) * mm, "end": v(-239.68, -58) * mm});
            skArc(sketch, "E299.MirrorCS", {"start": v(-246.42, -65.28) * mm, "mid": v(-247.39, -68.46) * mm, "end": v(-245.49, -71.2) * mm});
            skLineSegment(sketch, "E300.MirrorCS", {"start": v(-233.85, -58.28) * mm, "end": v(-223.3, -72.18) * mm});
            skArc(sketch, "E301.MirrorCS", {"start": v(-233, -48) * mm, "mid": v(-233.1, -51.32) * mm, "end": v(-230.55, -53.45) * mm});
            skLineSegment(sketch, "E302.MirrorCS", {"start": v(-233, -48) * mm, "end": v(-228.4, -39.2) * mm});
            skArc(sketch, "E303.MirrorCS", {"start": v(-222.7, -37.94) * mm, "mid": v(-225.84, -37.24) * mm, "end": v(-228.4, -39.2) * mm});
            skLineSegment(sketch, "E304.MirrorCS", {"start": v(-222.7, -37.94) * mm, "end": v(-208.87, -48.58) * mm});
            skLineSegment(sketch, "E305.MirrorCS", {"start": v(-213.41, -57.77) * mm, "end": v(-230.55, -53.45) * mm});
            skLineSegment(sketch, "E306.MirrorCS", {"start": v(-204.1, -31.1) * mm, "end": v(-221.75, -32.17) * mm});
            skArc(sketch, "E307.MirrorCS", {"start": v(-225.73, -27.7) * mm, "mid": v(-224.82, -30.9) * mm, "end": v(-221.75, -32.17) * mm});
            skLineSegment(sketch, "E308.MirrorCS", {"start": v(-225.73, -27.7) * mm, "end": v(-224, -17.93) * mm});
            skArc(sketch, "E309.MirrorCS", {"start": v(-218.95, -15.01) * mm, "mid": v(-222.16, -15.3) * mm, "end": v(-224, -17.93) * mm});
            skLineSegment(sketch, "E310.MirrorCS", {"start": v(-218.95, -15.01) * mm, "end": v(-202.55, -20.98) * mm});
            skLineSegment(sketch, "E311.MirrorCS", {"start": v(-251.54, -74.72) * mm, "end": v(-246.24, -91.35) * mm});
            skArc(sketch, "E312.MirrorCS", {"start": v(-233.85, -58.28) * mm, "mid": v(-236.7, -56.78) * mm, "end": v(-239.68, -58) * mm});
            skLineSegment(sketch, "E313.MirrorCS", {"start": v(-230.08, -79.85) * mm, "end": v(-245.49, -71.2) * mm});
            skLineSegment(sketch, "E314", {"start": v(221.78, 139.03) * mm, "end": v(211.23, 125.2) * mm});
            skLineSegment(sketch, "E315", {"start": v(205.28, 125.06) * mm, "end": v(198.9, 132.65) * mm});
            skLineSegment(sketch, "E316", {"start": v(199.98, 138.43) * mm, "end": v(215.11, 146.8) * mm});
            skPoint(sketch, "E317.visualSharp", {"position": v(217.86, 148.33) * mm});
            skPoint(sketch, "E318.visualSharp", {"position": v(223.62, 141.45) * mm});
            skArc(sketch, "E319.filletArc", {"start": v(205.28, 125.06) * mm, "mid": v(208.29, 123.7) * mm, "end": v(211.23, 125.2) * mm});
            skArc(sketch, "E320.filletArc", {"start": v(199.98, 138.43) * mm, "mid": v(198.08, 135.8) * mm, "end": v(198.9, 132.65) * mm});
            skLineSegment(sketch, "E321", {"start": v(-35.33, 146.4) * mm, "end": v(-20.14, 138.22) * mm});
            skLineSegment(sketch, "E322", {"start": v(-19.02, 132.42) * mm, "end": v(-25.42, 124.8) * mm});
            skLineSegment(sketch, "E323", {"start": v(-31.35, 124.9) * mm, "end": v(-41.94, 138.57) * mm});
            skPoint(sketch, "E324.visualSharp", {"position": v(-43.82, 141) * mm});
            skPoint(sketch, "E325.visualSharp", {"position": v(-38.06, 147.86) * mm});
            skArc(sketch, "E326.filletArc", {"start": v(-19.02, 132.42) * mm, "mid": v(-18.2, 135.59) * mm, "end": v(-20.14, 138.22) * mm});
            skArc(sketch, "E327.filletArc", {"start": v(-31.35, 124.9) * mm, "mid": v(-28.41, 123.43) * mm, "end": v(-25.42, 124.8) * mm});
            skLineSegment(sketch, "E328", {"start": v(-41.65, -73.44) * mm, "end": v(-31.12, -59.25) * mm});
            skLineSegment(sketch, "E329", {"start": v(-25.14, -59.07) * mm, "end": v(-18.76, -66.67) * mm});
            skLineSegment(sketch, "E330", {"start": v(-19.78, -72.42) * mm, "end": v(-34.89, -81.15) * mm});
            skPoint(sketch, "E331.visualSharp", {"position": v(-37.66, -82.75) * mm});
            skPoint(sketch, "E332.visualSharp", {"position": v(-43.44, -75.86) * mm});
            skArc(sketch, "E333.filletArc", {"start": v(-25.14, -59.07) * mm, "mid": v(-28.18, -57.7) * mm, "end": v(-31.12, -59.25) * mm});
            skArc(sketch, "E334.filletArc", {"start": v(-19.78, -72.42) * mm, "mid": v(-17.93, -69.78) * mm, "end": v(-18.76, -66.67) * mm});
            skLineSegment(sketch, "E335", {"start": v(215.98, -81.18) * mm, "end": v(200.17, -73.28) * mm});
            skLineSegment(sketch, "E336", {"start": v(198.96, -67.43) * mm, "end": v(205.34, -59.82) * mm});
            skLineSegment(sketch, "E337", {"start": v(211.17, -59.82) * mm, "end": v(222.4, -73.19) * mm});
            skPoint(sketch, "E338.visualSharp", {"position": v(224.45, -75.64) * mm});
            skPoint(sketch, "E339.visualSharp", {"position": v(218.67, -82.53) * mm});
            skArc(sketch, "E340.filletArc", {"start": v(198.96, -67.43) * mm, "mid": v(198.14, -70.65) * mm, "end": v(200.17, -73.28) * mm});
            skArc(sketch, "E341.filletArc", {"start": v(211.17, -59.82) * mm, "mid": v(208.26, -58.46) * mm, "end": v(205.34, -59.82) * mm});
            skArc(sketch, "E342", {"start": v(-66.15, 99.78) * mm, "mid": v(-71.7, 96.24) * mm, "end": v(-69.4, 90.07) * mm});
            skArc(sketch, "E343", {"start": v(-53.37, 123.14) * mm, "mid": v(-59.51, 120.78) * mm, "end": v(-58.48, 114.27) * mm});
            skArc(sketch, "E344", {"start": v(-35.33, 146.4) * mm, "mid": v(-41.8, 145.16) * mm, "end": v(-41.94, 138.57) * mm});
            skArc(sketch, "E345", {"start": v(-13.44, 167.4) * mm, "mid": v(-20.02, 167.4) * mm, "end": v(-21.43, 160.98) * mm});
            skArc(sketch, "E346", {"start": v(9.38, 182.48) * mm, "mid": v(2.9, 183.64) * mm, "end": v(0.4, 177.55) * mm});
            skArc(sketch, "E347", {"start": v(33.31, 192.78) * mm, "mid": v(27.14, 195.08) * mm, "end": v(23.6, 189.53) * mm});
            skArc(sketch, "E348", {"start": v(-74.04, 75.96) * mm, "mid": v(-79.11, 71.76) * mm, "end": v(-76.08, 65.92) * mm});
            skArc(sketch, "E349", {"start": v(-78.98, 50.92) * mm, "mid": v(-83.44, 46.07) * mm, "end": v(-79.65, 40.7) * mm});
            skArc(sketch, "E350", {"start": v(57.47, 199.46) * mm, "mid": v(51.62, 202.5) * mm, "end": v(47.42, 197.43) * mm});
            skArc(sketch, "E351", {"start": v(82.69, 203.03) * mm, "mid": v(77.3, 206.82) * mm, "end": v(72.47, 202.36) * mm});
            skArc(sketch, "E352.MirrorCS", {"start": v(98.12, 203.03) * mm, "mid": v(103.5, 206.82) * mm, "end": v(108.35, 202.36) * mm});
            skArc(sketch, "E353.MirrorCS", {"start": v(123.35, 199.46) * mm, "mid": v(129.19, 202.5) * mm, "end": v(133.39, 197.43) * mm});
            skArc(sketch, "E354.MirrorCS", {"start": v(147.5, 192.78) * mm, "mid": v(153.67, 195.08) * mm, "end": v(157.21, 189.53) * mm});
            skArc(sketch, "E355.MirrorCS", {"start": v(171.43, 182.48) * mm, "mid": v(177.91, 183.64) * mm, "end": v(180.42, 177.55) * mm});
            skArc(sketch, "E356.MirrorCS", {"start": v(194.25, 167.4) * mm, "mid": v(200.83, 167.4) * mm, "end": v(202.24, 160.98) * mm});
            skArc(sketch, "E357.MirrorCS", {"start": v(246.96, 99.78) * mm, "mid": v(252.5, 96.24) * mm, "end": v(250.21, 90.07) * mm});
            skArc(sketch, "E358.MirrorCS", {"start": v(254.86, 75.96) * mm, "mid": v(259.93, 71.76) * mm, "end": v(256.9, 65.92) * mm});
            skArc(sketch, "E359.MirrorCS", {"start": v(259.8, 50.92) * mm, "mid": v(264.25, 46.07) * mm, "end": v(260.46, 40.7) * mm});
            skArc(sketch, "E360", {"start": v(221.78, 139.03) * mm, "mid": v(221.61, 145.63) * mm, "end": v(215.11, 146.8) * mm});
            skArc(sketch, "E361", {"start": v(239.91, 114) * mm, "mid": v(241.07, 120.48) * mm, "end": v(234.98, 122.99) * mm});
            skArc(sketch, "E362.MirrorCS", {"start": v(-78.98, 15.04) * mm, "mid": v(-83.44, 19.88) * mm, "end": v(-79.65, 25.26) * mm});
            skArc(sketch, "E363.MirrorCS", {"start": v(-74.04, -10) * mm, "mid": v(-79.11, -5.8) * mm, "end": v(-76.08, 0.04) * mm});
            skArc(sketch, "E364.MirrorCS", {"start": v(-66.15, -33.83) * mm, "mid": v(-71.7, -30.29) * mm, "end": v(-69.4, -24.12) * mm});
            skArc(sketch, "E365.MirrorCS", {"start": v(-13.44, -101.44) * mm, "mid": v(-20.02, -101.46) * mm, "end": v(-21.43, -95.03) * mm});
            skArc(sketch, "E366.MirrorCS", {"start": v(9.38, -116.53) * mm, "mid": v(2.9, -117.69) * mm, "end": v(0.4, -111.6) * mm});
            skArc(sketch, "E367.MirrorCS", {"start": v(33.31, -126.83) * mm, "mid": v(27.14, -129.13) * mm, "end": v(23.6, -123.58) * mm});
            skArc(sketch, "E368.MirrorCS", {"start": v(57.47, -133.51) * mm, "mid": v(51.62, -136.54) * mm, "end": v(47.42, -131.47) * mm});
            skArc(sketch, "E369.MirrorCS", {"start": v(82.69, -137.08) * mm, "mid": v(77.3, -140.87) * mm, "end": v(72.47, -136.41) * mm});
            skArc(sketch, "E370.MirrorCS", {"start": v(98.12, -137.08) * mm, "mid": v(103.5, -140.87) * mm, "end": v(108.35, -136.41) * mm});
            skArc(sketch, "E371.MirrorCS", {"start": v(123.35, -133.51) * mm, "mid": v(129.19, -136.54) * mm, "end": v(133.39, -131.47) * mm});
            skArc(sketch, "E372.MirrorCS", {"start": v(147.5, -126.83) * mm, "mid": v(153.67, -129.13) * mm, "end": v(157.21, -123.58) * mm});
            skArc(sketch, "E373.MirrorCS", {"start": v(171.43, -116.53) * mm, "mid": v(177.91, -117.69) * mm, "end": v(180.42, -111.6) * mm});
            skArc(sketch, "E374.MirrorCS", {"start": v(194.25, -101.44) * mm, "mid": v(200.83, -101.46) * mm, "end": v(202.24, -95.03) * mm});
            skArc(sketch, "E375.MirrorCS", {"start": v(239.91, -48.05) * mm, "mid": v(241.07, -54.53) * mm, "end": v(234.98, -57.04) * mm});
            skArc(sketch, "E376.MirrorCS", {"start": v(246.96, -33.83) * mm, "mid": v(252.5, -30.29) * mm, "end": v(250.21, -24.12) * mm});
            skArc(sketch, "E377.MirrorCS", {"start": v(254.86, -10) * mm, "mid": v(259.93, -5.8) * mm, "end": v(256.9, 0.04) * mm});
            skArc(sketch, "E378.MirrorCS", {"start": v(259.8, 15.04) * mm, "mid": v(264.25, 19.88) * mm, "end": v(260.46, 25.26) * mm});
            skArc(sketch, "E379", {"start": v(-59.1, -48.05) * mm, "mid": v(-60.32, -54.57) * mm, "end": v(-54.17, -57.04) * mm});
            skArc(sketch, "E380", {"start": v(-41.65, -73.44) * mm, "mid": v(-41.43, -80.07) * mm, "end": v(-34.89, -81.15) * mm});
            skArc(sketch, "E381", {"start": v(215.98, -81.18) * mm, "mid": v(222.41, -79.77) * mm, "end": v(222.4, -73.19) * mm});
            skArc(sketch, "E382", {"start": v(-246.24, 67.65) * mm, "mid": v(-248.73, 73.75) * mm, "end": v(-255.21, 72.6) * mm});
            skArc(sketch, "E383", {"start": v(-223.3, 48.48) * mm, "mid": v(-223.54, 55.1) * mm, "end": v(-230.08, 56.15) * mm});
            skArc(sketch, "E384", {"start": v(-208.87, 24.89) * mm, "mid": v(-207.44, 31.31) * mm, "end": v(-213.41, 34.07) * mm});
            skArc(sketch, "E385", {"start": v(-202.55, -2.72) * mm, "mid": v(-199.17, 2.99) * mm, "end": v(-204.1, 7.41) * mm});
            skArc(sketch, "E386", {"start": v(-276.67, 77.95) * mm, "mid": v(-281.3, 82.7) * mm, "end": v(-286.86, 79.07) * mm});
            skArc(sketch, "E387", {"start": v(-302.17, 79.14) * mm, "mid": v(-307.67, 82.77) * mm, "end": v(-312.37, 78.14) * mm});
            skArc(sketch, "E388", {"start": v(-333.8, 72.69) * mm, "mid": v(-340.27, 73.92) * mm, "end": v(-342.82, 67.84) * mm});
            skArc(sketch, "E389", {"start": v(-358.91, 56.25) * mm, "mid": v(-365.45, 55.26) * mm, "end": v(-365.8, 48.66) * mm});
            skArc(sketch, "E390", {"start": v(-375.59, 34.19) * mm, "mid": v(-381.63, 31.5) * mm, "end": v(-380.22, 25.05) * mm});
            skArc(sketch, "E391", {"start": v(-384.91, 7.54) * mm, "mid": v(-389.85, 3.15) * mm, "end": v(-386.54, -2.57) * mm});
            skArc(sketch, "E392", {"start": v(-386.75, -20.98) * mm, "mid": v(-390.06, -26.67) * mm, "end": v(-385.2, -31.1) * mm});
            skArc(sketch, "E393", {"start": v(-380.43, -48.58) * mm, "mid": v(-381.86, -55) * mm, "end": v(-375.89, -57.77) * mm});
            skArc(sketch, "E394", {"start": v(-366, -72.18) * mm, "mid": v(-365.7, -78.75) * mm, "end": v(-359.22, -79.85) * mm});
            skArc(sketch, "E395", {"start": v(-343.06, -91.35) * mm, "mid": v(-340.57, -97.44) * mm, "end": v(-334.09, -96.3) * mm});
            skArc(sketch, "E396", {"start": v(-312.63, -101.65) * mm, "mid": v(-308, -106.39) * mm, "end": v(-302.44, -102.77) * mm});
            skArc(sketch, "E397", {"start": v(-286.86, -102.77) * mm, "mid": v(-281.31, -106.32) * mm, "end": v(-276.67, -101.65) * mm});
            skArc(sketch, "E398", {"start": v(-255.21, -96.3) * mm, "mid": v(-248.7, -97.5) * mm, "end": v(-246.24, -91.35) * mm});
            skArc(sketch, "E399", {"start": v(-230.08, -79.85) * mm, "mid": v(-223.6, -78.75) * mm, "end": v(-223.3, -72.18) * mm});
            skArc(sketch, "E400", {"start": v(-213.41, -57.77) * mm, "mid": v(-207.37, -55.04) * mm, "end": v(-208.87, -48.58) * mm});
            skArc(sketch, "E401", {"start": v(-204.1, -31.1) * mm, "mid": v(-199.17, -26.68) * mm, "end": v(-202.55, -20.98) * mm});
            skSolve(sketch);
        }
        {
            var Q0;
            Q0 = qSketchRegion(id + "F0", true);
            extrude(context, id + "F1", {"entities" : qUnion([Q0]), "depth" : 25.4 * mm});
        }
    });
